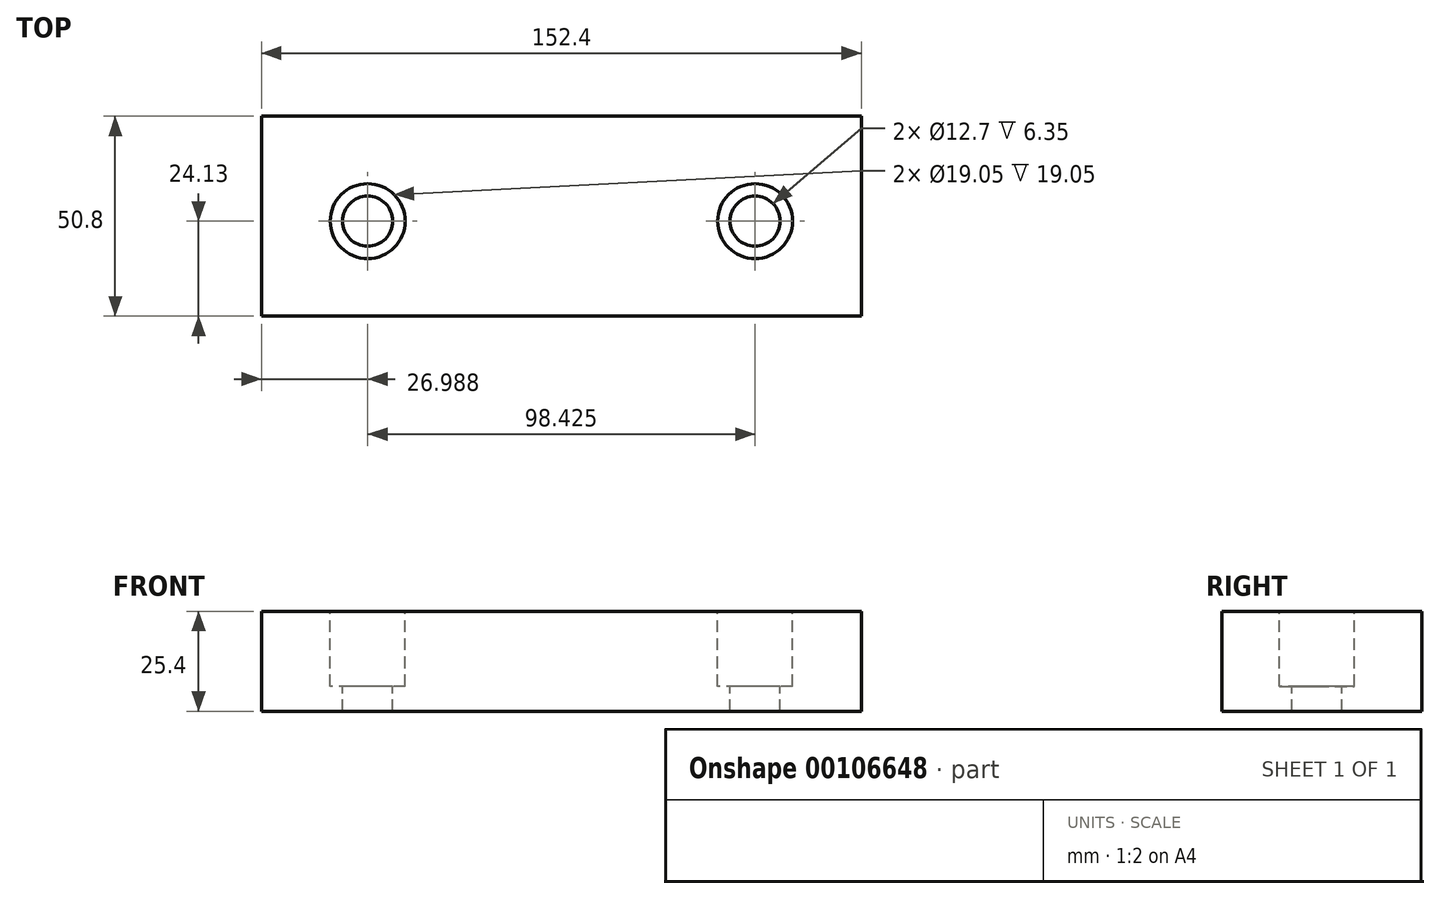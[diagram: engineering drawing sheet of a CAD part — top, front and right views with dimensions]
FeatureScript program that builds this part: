
annotation { "Feature Type Name" : "Feature", "Feature Type Description" : "" }
export const myFeature = defineFeature(function(context is Context, id is Id, definition is map)
    precondition{}
    {
        {
            var Q0;
            Q0=qCreatedBy(makeId("Top.planeOp"),FACE);
            var sketch = newSketch(context, id + "F0", { "sketchPlane" : qUnion([Q0])});
            skLineSegment(sketch, "E0.bottom", {"start": v(76.2, -25.4) * mm, "end": v(-76.2, -25.4) * mm});
            skLineSegment(sketch, "E0.top", {"start": v(76.2, 25.4) * mm, "end": v(-76.2, 25.4) * mm});
            skLineSegment(sketch, "E0.left", {"start": v(76.2, -25.4) * mm, "end": v(76.2, 25.4) * mm});
            skLineSegment(sketch, "E0.right", {"start": v(-76.2, -25.4) * mm, "end": v(-76.2, 25.4) * mm});
            skPoint(sketch, "E0.middle", {"position": v(0, 0) * mm});
            skLineSegment(sketch, "E1", {"start": v(0, -25.4) * mm, "end": v(0, -1.27) * mm});
            skLineSegment(sketch, "E2", {"start": v(0, -1.27) * mm, "end": v(49.21, -1.27) * mm});
            skLineSegment(sketch, "E3", {"start": v(0, -1.27) * mm, "end": v(-49.21, -1.27) * mm});
            skCircle(sketch, "E4", {"center": v(-49.21, -1.27) * mm, "radius": 6.35 * mm});
            skCircle(sketch, "E5", {"center": v(49.21, -1.27) * mm, "radius": 6.35 * mm});
            skSolve(sketch);
        }
        {
            var Q0;
            Q0=makeQuery(id+"F0.imprint","IMPRINT",FACE,{"disambiguationData":[TD([[makeQuery(id+"F0.imprint","IMPRINT",EDGE,{"derivedFrom":sQuery(id+"F0.wireOp",EDGE,"E0.top")}),1.0]])]});
            extrude(context, id + "F1", {"entities" : qUnion([Q0]), "oppositeDirection" : true, "depth" : 25.4 * mm});
        }
        {
            var Q0;
            Q0=makeQuery(id+"F1.opExtrude","CAP_FACE",FACE,{"disambiguationData":[OSD([sQuery(id+"F0.wireOp",EDGE,"E0.bottom"),sQuery(id+"F0.wireOp",EDGE,"E0.top"),sQuery(id+"F0.wireOp",EDGE,"E0.left"),sQuery(id+"F0.wireOp",EDGE,"E0.right"),sQuery(id+"F0.wireOp",EDGE,"E4"),sQuery(id+"F0.wireOp",EDGE,"E5")])],"isStart":true});
            var sketch = newSketch(context, id + "F2", { "sketchPlane" : qUnion([Q0])});
            skCircle(sketch, "E6", {"center": v(-49.21, -1.27) * mm, "radius": 9.53 * mm});
            skCircle(sketch, "E7", {"center": v(49.21, -1.27) * mm, "radius": 9.53 * mm});
            skSolve(sketch);
        }
        {
            var Q0;
            Q0 = qSketchRegion(id + "F2", true);
            extrude(context, id + "F3", {"entities" : qUnion([Q0]), "operationType" : NewBodyOperationType.REMOVE, "oppositeDirection" : true, "depth" : 19.05 * mm});
        }
    });
